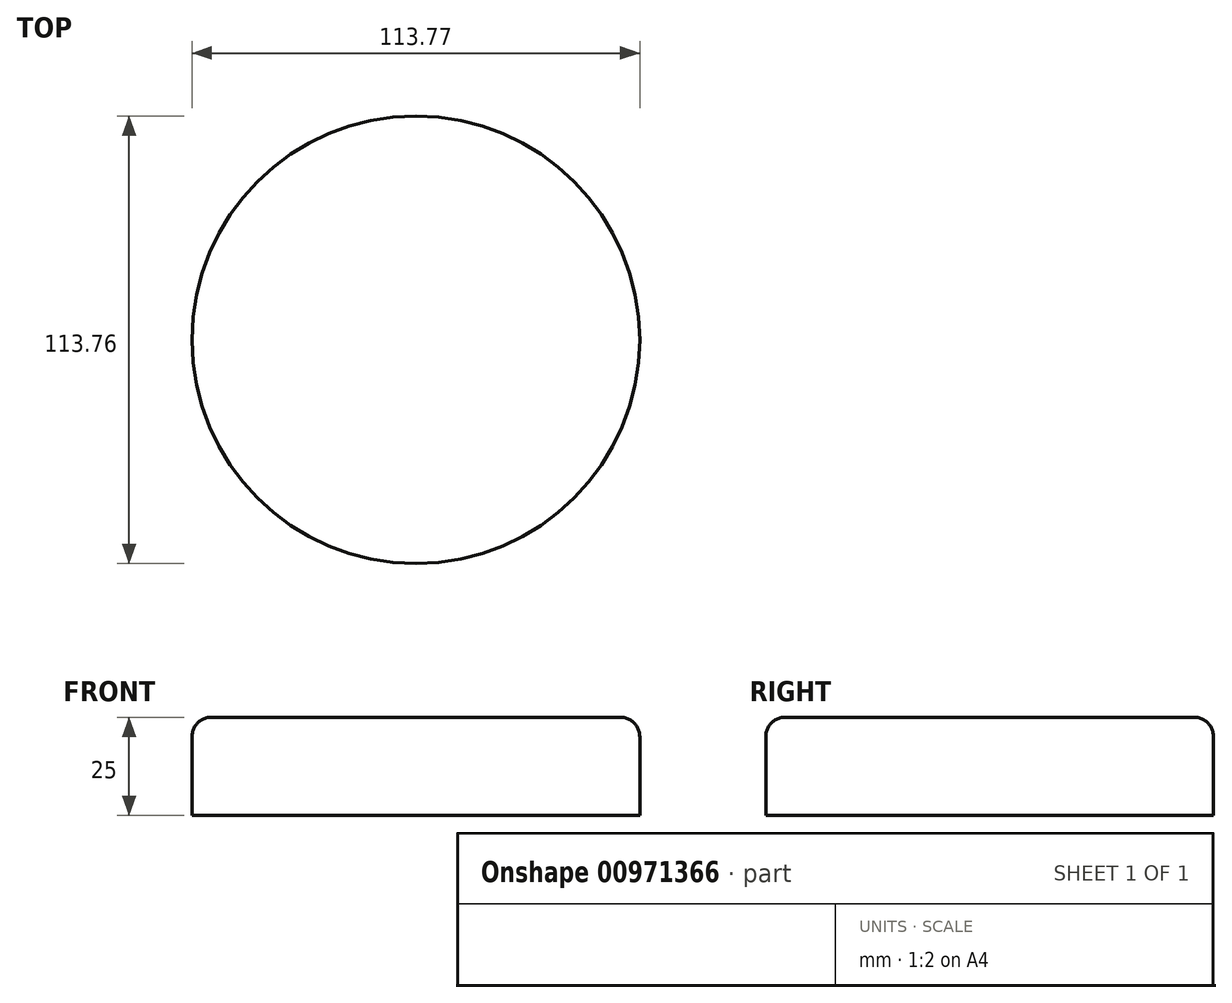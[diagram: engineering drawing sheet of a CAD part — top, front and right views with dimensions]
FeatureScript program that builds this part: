
annotation { "Feature Type Name" : "Feature", "Feature Type Description" : "" }
export const myFeature = defineFeature(function(context is Context, id is Id, definition is map)
    precondition{}
    {
        {
            var Q0;
            Q0=qCreatedBy(makeId("Top.planeOp"),FACE);
            var sketch = newSketch(context, id + "F0", { "sketchPlane" : qUnion([Q0])});
            skCircle(sketch, "E0", {"center": v(-42.5, 68.91) * mm, "radius": 56.88 * mm});
            skPoint(sketch, "E0.first.point", {"position": v(10.97, 49.53) * mm});
            skPoint(sketch, "E0.second.point", {"position": v(12.6, 54.83) * mm});
            skPoint(sketch, "E0.third.point", {"position": v(0, 31.11) * mm});
            skSolve(sketch);
        }
        {
            var Q0;
            Q0=makeQuery(id+"F0.imprint","IMPRINT",FACE,{"disambiguationData":[TD([[makeQuery(id+"F0.imprint","IMPRINT",EDGE,{"derivedFrom":sQuery(id+"F0.wireOp",EDGE,"E0")}),1.0]])]});
            extrude(context, id + "F1", {"entities" : qUnion([Q0]), "depth" : 25 * mm, "offsetDistance" : 25 * mm});
        }
        {
            var Q0;
            Q0=makeQuery(id+"F1.opExtrude","CAP_EDGE",EDGE,{"disambiguationData":[OSD([sQuery(id+"F0.wireOp",EDGE,"E0")])],"isStart":false});
            fillet(context, id + "F2", {"entities" : qUnion([Q0]), "radius" : 5 * mm, "tangentPropagation" : true, "allowEdgeOverflow" : false});
        }
    });
